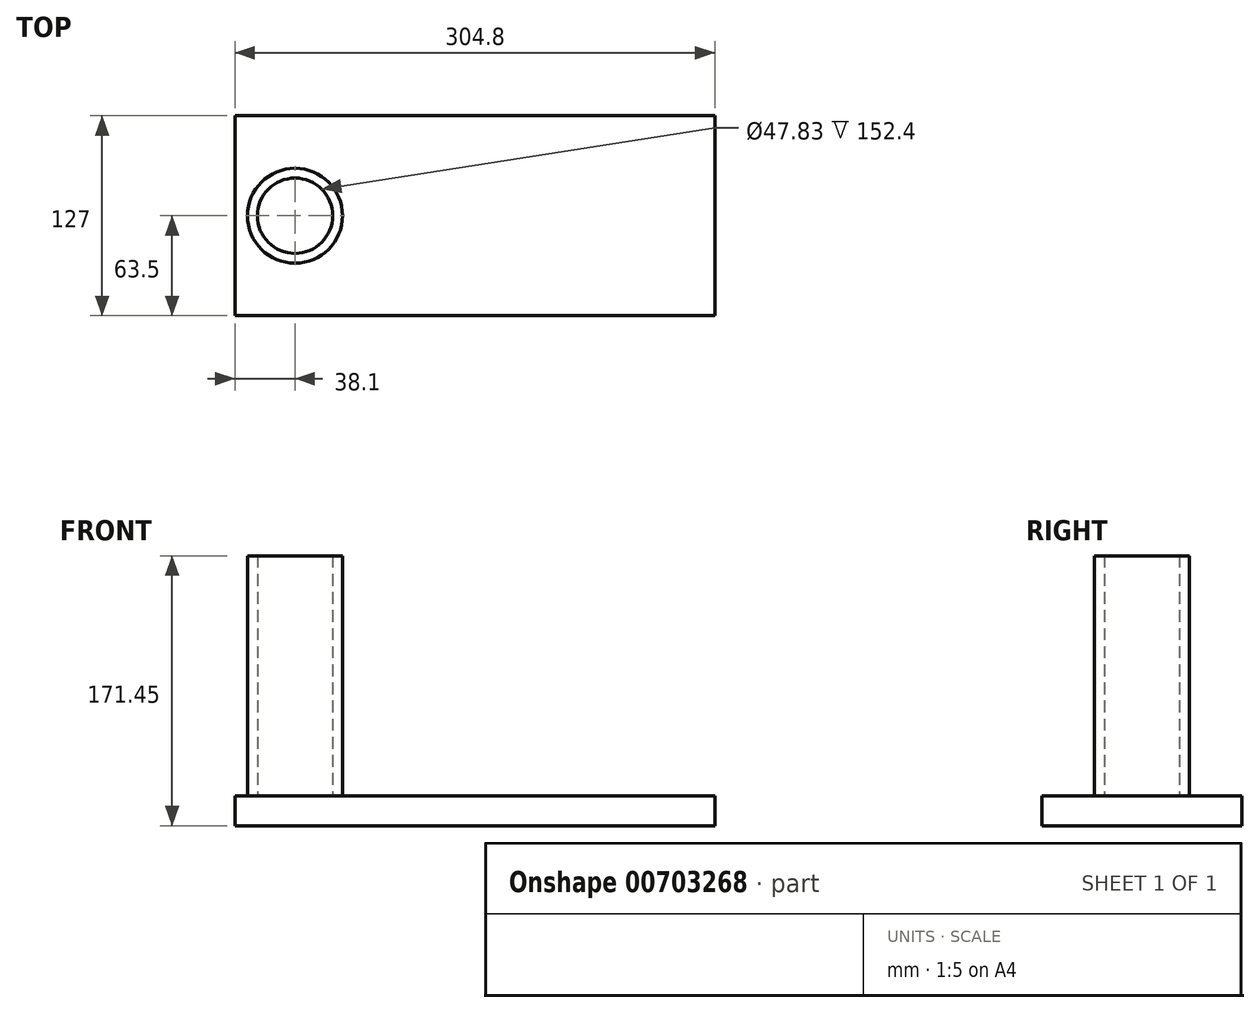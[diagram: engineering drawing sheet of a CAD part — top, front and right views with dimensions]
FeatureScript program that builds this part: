
annotation { "Feature Type Name" : "Feature", "Feature Type Description" : "" }
export const myFeature = defineFeature(function(context is Context, id is Id, definition is map)
    precondition{}
    {
        {
            var Q0;
            Q0=qCreatedBy(makeId("Top.planeOp"),FACE);
            var sketch = newSketch(context, id + "F0", { "sketchPlane" : qUnion([Q0])});
            skLineSegment(sketch, "E0.bottom", {"start": v(152.4, -63.5) * mm, "end": v(-152.4, -63.5) * mm});
            skLineSegment(sketch, "E0.top", {"start": v(152.4, 63.5) * mm, "end": v(-152.4, 63.5) * mm});
            skLineSegment(sketch, "E0.left", {"start": v(152.4, -63.5) * mm, "end": v(152.4, 63.5) * mm});
            skLineSegment(sketch, "E0.right", {"start": v(-152.4, -63.5) * mm, "end": v(-152.4, 63.5) * mm});
            skPoint(sketch, "E0.middle", {"position": v(0, 0) * mm});
            skSolve(sketch);
        }
        {
            var Q0;
            Q0 = qSketchRegion(id + "F0", true);
            extrude(context, id + "F1", {"entities" : qUnion([Q0]), "depth" : 19.05 * mm, "offsetDistance" : 25.4 * mm});
        }
        {
            var Q0;
            Q0=makeQuery(id+"F1.opExtrude","CAP_FACE",FACE,{"disambiguationData":[OSD([sQuery(id+"F0.wireOp",EDGE,"E0.bottom"),sQuery(id+"F0.wireOp",EDGE,"E0.top"),sQuery(id+"F0.wireOp",EDGE,"E0.left"),sQuery(id+"F0.wireOp",EDGE,"E0.right")])],"isStart":false});
            var sketch = newSketch(context, id + "F2", { "sketchPlane" : qUnion([Q0])});
            skCircle(sketch, "E1", {"center": v(-114.3, 0) * mm, "radius": 30.16 * mm});
            skCircle(sketch, "E2", {"center": v(-114.3, 0) * mm, "radius": 23.91 * mm});
            skSolve(sketch);
        }
        {
            var Q0;
            Q0=makeQuery(id+"F2.imprint","IMPRINT",FACE,{"disambiguationData":[TD([[makeQuery(id+"F2.imprint","IMPRINT",EDGE,{"derivedFrom":sQuery(id+"F2.wireOp",EDGE,"E1")}),1.0]])]});
            extrude(context, id + "F3", {"entities" : qUnion([Q0]), "operationType" : NewBodyOperationType.ADD, "depth" : 152.4 * mm, "offsetDistance" : 25.4 * mm});
        }
    });
